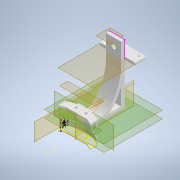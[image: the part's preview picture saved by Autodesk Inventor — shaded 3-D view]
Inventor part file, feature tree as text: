
AUTODESK INVENTOR PART (.ipt)
format: ipt  version: 2021 (Build 250183000, 183)  size: 5,319,168 bytes
history: native  units: mm
features: sketch x34, move_body x21, extrude x20, other x20, direct_edit x20, plane x14, projected_geometry x13, delete_face x8, mirror x6, fillet x6, sweep x2, revolve x2, thread x1
ambient origin geometry x8: Origin, YZ Plane, XZ Plane, XY Plane, X Axis, Y Axis, Z Axis, Center Point
bodies: Solid1 (feature_tree), Solid2 (feature_tree), Solid3 (feature_tree), Solid4 (feature_tree), Solid5 (feature_tree), Solid6 (feature_tree)
feature tree (167):
  sketch  "Sketch7"  dims[d10=10.0mm d11=31.4mm]
  plane  "Work Plane4"
  sketch  "Sketch8"  dims[d13=100.0mm d33=100.0mm]
  plane  "Work Plane5"
  plane  "Work Plane7"
  mirror  "Mirror4"
  sweep  "Sweep5"
  sketch  "Sketch15"  dims[d38=7.0mm d39=1.0mm]
  plane  "Work Plane13"
  extrude  "Extrusion7"  Depth=100.0mm
  mirror  "Mirror6"
  mirror  "Mirror7"
  extrude  "Extrusion8"  Depth=100.0mm
  plane  "Work Plane14"
  mirror  "Mirror8"
  mirror  "Mirror9"
  extrude  "Extrusion9"  Depth=1.0mm
  sketch  "Sketch18"  dims[d45=3.5mm d46=1.0mm]
  plane  "Work Plane15"
  plane  "Work Plane16"
  plane  "Work Plane17"
  extrude  "Extrusion11"  Depth=1.0mm
  fillet  "Fillet5"  Radius=9.0mm
  plane  "Work Plane20"
  mirror  "Mirror10"
  extrude  "Extrusion12"  Depth=1.0mm
  sweep  "Sweep6"
  extrude  "Extrusion13"  Depth=5.0mm
  fillet  "Fillet7"  Radius=1.0mm
  extrude  "Extrusion14"  TaperAngle=0.0deg  [1 undecoded]
  extrude  "Extrusion15"  Depth=1.0mm TaperAngle=0.0deg
  fillet  "Fillet8"  Radius=3.0mm
  extrude  "Extrusion16"  Depth=38.5mm TaperAngle=0.0deg
  extrude  "Extrusion17"  Depth=2.0mm
  extrude  "Extrusion18"  Depth=166.75mm TaperAngle=0.0deg
  extrude  "Extrusion19"  Depth=2.0mm TaperAngle=0.0deg
  extrude  "Extrusion20"  Depth=13.25mm TaperAngle=0.0deg
  extrude  "Extrusion21"  Depth=2.0mm
  sketch  "Sketch32"  dims[d125=-36.254mm d126=16.5mm d127=86.882mm d128=-1.25mm d129=0.0mm d130=0.0mm]
  plane  "Work Plane22"
  sketch  "Sketch33"  dims[d131=0.0mm d132=0.0mm d133=0.1mm d136=0.0mm d137=0.0mm d138=51.5mm]
  plane  "Work Plane23"
  extrude  "Extrusion22"  Depth=13.25mm TaperAngle=0.0deg
  fillet  "Fillet9"  Radius=5.5mm
  sketch  "Sketch34"  dims[d139=10.0mm d140=0.0mm d141=10.0mm d142=0.0mm]
  other  "Split2[2]"
  thread  "Thread1"  [1 undecoded]
  other  "Cut-Extrude10[1]"
  other  "Cut-Extrude10[2]"
  other  "Cut-Extrude12"
  direct_edit  "Direct Edit1"
  direct_edit  "Direct Edit2"
  direct_edit  "Direct Edit3"
  sketch  "Sketch35"  dims[d145=2.0mm d146=-4.75mm]
  direct_edit  "Direct Edit4"
  sketch  "Sketch37"  dims[d148=1.5mm]
  direct_edit  "Direct Edit5"
  extrude  "Extrusion24"  Depth=10.0mm
  plane  "Work Plane24"
  extrude  "Extrusion25"  Depth=10.0mm TaperAngle=0.0deg
  delete_face  "Delete Face1"
  delete_face  "Delete Face2"
  delete_face  "Delete Face3"
  delete_face  "Delete Face4"
  delete_face  "Delete Face5"
  delete_face  "Delete Face6"
  delete_face  "Delete Face7"
  delete_face  "Delete Face8"
  fillet  "Fillet10"  Radius=2.0mm
  direct_edit  "Direct Edit7"
  direct_edit  "Direct Edit8"
  extrude  "Extrusion27"  Depth=31.4mm
  fillet  "Fillet11"  Radius=31.4mm
  direct_edit  "Direct Edit9"
  direct_edit  "Direct Edit10"
  direct_edit  "Direct Edit11"
  direct_edit  "Direct Edit12"
  direct_edit  "Direct Edit13"
  direct_edit  "Direct Edit14"
  direct_edit  "Direct Edit15"
  direct_edit  "Direct Edit16"
  direct_edit  "Direct Edit17"
  direct_edit  "Direct Edit18"
  sketch  "Sketch42"  dims[d152=1.5mm]
  direct_edit  "Direct Edit19"
  extrude  "Extrusion28"  TaperAngle=0.0deg  [1 undecoded]
  sketch  "Sketch36"  dims[d147=-7.25mm]
  extrude  "Extrusion29"  Depth=51.5mm TaperAngle=0.0deg
  direct_edit  "Direct Edit20"
  direct_edit  "Direct Edit21"
  sketch  "Sketch44"  dims[d155=2.0mm]
  sketch  "Sketch45"  dims[d156=1.25mm]
  sketch  "Sketch46"  dims[d157=1.25mm d158=0.0mm d159=0.0mm d160=-1.25mm d161=0.0mm d162=0.0mm d163=-0.25mm d164=0.0mm d165=0.0mm d166=1.0mm d167=-0.5mm d168=0.0mm d169=0.0mm d170=1.75mm d171=0.0mm d172=0.0mm d173=4.0mm d174=0.0mm d175=-2.5mm d176=0.0mm d177=0.0mm d178=0.0mm d179=-46.5mm d180=0.0mm d181=0.0mm d182=-46.5mm d183=0.0mm d184=0.0mm d185=-1.0mm d186=0.0mm d187=0.0mm d188=-0.5mm d189=0.0mm d190=0.0mm d191=1.5mm d192=0.0mm d193=0.0mm d194=-6.5mm d195=0.0mm d196=0.0mm d197=-4.5mm d198=0.0mm d199=0.0mm d200=-0.5mm d201=0.0mm d202=0.0mm d203=-0.5mm d204=0.0mm d205=0.0mm d206=0.5mm d207=0.0mm d208=0.0mm d209=0.5mm d210=6.0mm d211=90.0mm d212=10.0mm d213=0.0mm d214=10.0mm d215=0.0mm d216=-4.0mm d217=-0.5mm]
  plane  "Work Plane9"
  sketch  "Sketch13"  dims[d36=100.0mm d37=100.0mm]
  projected_geometry  "Projected Loop5"
  sketch  "Sketch16"  dims[d40=9.0mm d41=1.0mm d42=9.0mm]
  sketch  "Sketch17"  dims[d43=3.5mm d44=1.0mm]
  sketch  "Sketch19"  dims[d47=1.0mm d48=5.0mm d49=1.0mm]
  sketch  "Sketch20"  dims[d50=5.0mm d71=0.0mm d72=0.0mm]
  sketch  "Sketch21"  dims[d75=1.0mm d76=0.0mm d77=1.0mm d78=0.0mm d79=3.0mm]
  sketch  "Sketch22"  dims[d80=3.0mm d81=38.5mm d82=0.0mm]
  sketch  "Sketch23"  dims[d85=2.0mm d86=2.0mm d87=0.0mm d88=0.0mm d89=2.0mm]
  projected_geometry  "Projected Loop10"
  projected_geometry  "Projected Loop11"
  sketch  "Sketch24"  dims[d92=25.0mm d93=166.75mm d94=0.0mm]
  projected_geometry  "Projected Loop12"
  sketch  "Sketch25"  dims[d95=0.0mm d96=0.0mm d98=2.0mm d99=0.0mm]
  sketch  "Sketch26"  dims[d100=2.0mm d101=13.25mm d102=0.0mm]
  sketch  "Sketch27"  dims[d103=13.25mm d104=0.0mm d105=2.0mm]
  projected_geometry  "Projected Loop13"
  sketch  "Sketch28"  dims[d106=13.25mm d107=0.0mm d108=13.25mm d109=0.0mm d110=5.5mm d111=0.0mm d112=0.0mm d113=0.0mm]
  projected_geometry  "Projected Loop14"
  projected_geometry  "Projected Loop15"
  sketch  "Sketch29"  dims[d114=10.0mm d115=0.0mm d116=5.5mm]
  sketch  "Sketch30"  dims[d117=10.0mm d118=0.0mm d119=10.0mm d120=0.0mm d121=2.0mm]
  sketch  "Sketch31"  dims[d122=6.9mm d123=31.4mm d124=31.4mm]
  plane  "Work Plane21"
  projected_geometry  "Projected Loop16"
  projected_geometry  "Projected Loop17"
  sketch  "Sketch38"  dims[d149=1.5mm]
  projected_geometry  "Projected Loop18"
  sketch  "Sketch39"  dims[d150=1.5mm]
  projected_geometry  "Projected Loop19"
  sketch  "Sketch41"  dims[d151=1.5mm]
  sketch  "Sketch43"  dims[d153=10.0mm d154=0.0mm]
  projected_geometry  "Projected Loop21"
  projected_geometry  "Projected Loop22"
  other  "Cavity6"
  revolve  "Rotate1"  [1 undecoded]
  revolve  "Rotate2"  [1 undecoded]
  move_body  "Move1"
  move_body  "Move2"
  move_body  "Move3"
  move_body  "Move4"
  other  "Size1"
  other  "Size2"
  other  "Size3"
  other  "Size4"
  other  "Size5"
  other  "Size6"
  other  "Size7"
  other  "Size8"
  other  "Size9"
  move_body  "Move5"
  move_body  "Move6"
  move_body  "Move7"
  other  "Size10"
  move_body  "Move8"
  move_body  "Move9"
  move_body  "Move10"
  move_body  "Move11"
  move_body  "Move12"
  move_body  "Move13"
  move_body  "Move14"
  move_body  "Move15"
  move_body  "Move16"
  move_body  "Move17"
  move_body  "Move18"
  move_body  "Move19"
  move_body  "Move20"
  move_body  "Move21"
  other  "Size11"
  other  "Size12"
  parser-record x1  (decoder bookkeeping rows leaked as tree rows — omitted from the tree; the rows remain in map.json)
  other  "whole_assembly.iam"
  other  "Intel Realsense D435:1"
note: 5 required parameter values undecoded (feature->parameter linkage not recoverable at this tier; creation-order binding heuristic only, values carry confidence <= 0.55)
note: 1 file-system path scrubbed to <path> (originals preserved in map.json)